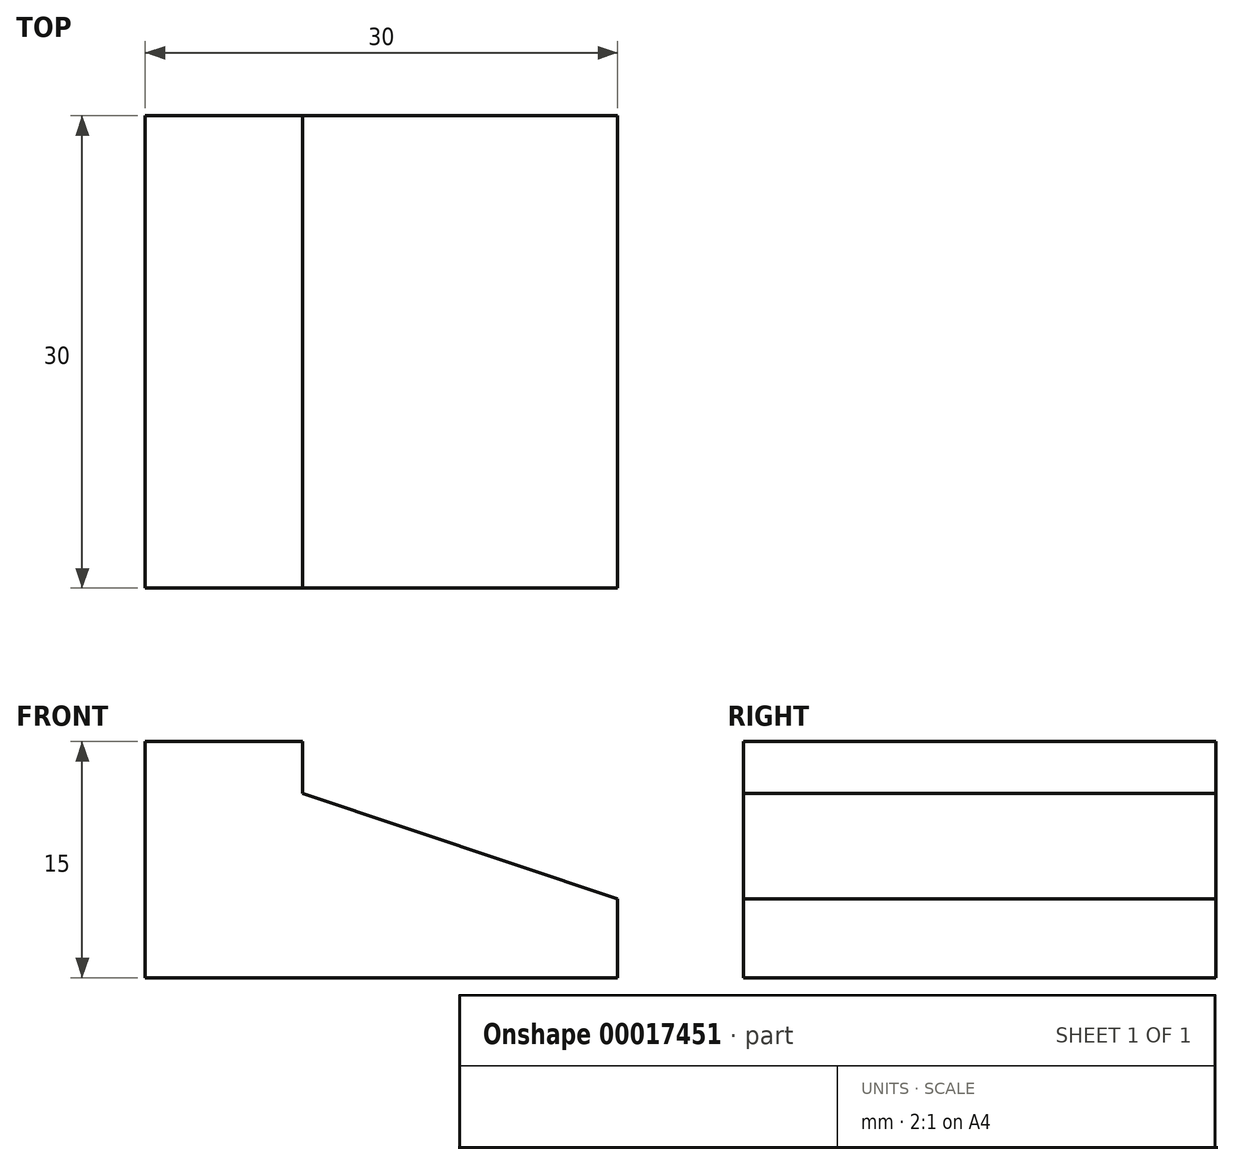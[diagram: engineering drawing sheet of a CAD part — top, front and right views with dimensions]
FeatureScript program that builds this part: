
annotation { "Feature Type Name" : "Feature", "Feature Type Description" : "" }
export const myFeature = defineFeature(function(context is Context, id is Id, definition is map)
    precondition{}
    {
        {
            var Q0;
            Q0=qCreatedBy(makeId("Front.planeOp"),FACE);
            var sketch = newSketch(context, id + "F0", { "sketchPlane" : qUnion([Q0])});
            skLineSegment(sketch, "E0", {"start": v(-16.89, 15) * mm, "end": v(-16.89, 0) * mm});
            skLineSegment(sketch, "E1", {"start": v(-16.89, 15) * mm, "end": v(-6.89, 15) * mm});
            skLineSegment(sketch, "E2", {"start": v(-16.89, 0) * mm, "end": v(13.11, 0) * mm});
            skLineSegment(sketch, "E3", {"start": v(-6.89, 15) * mm, "end": v(-6.89, 11.72) * mm});
            skLineSegment(sketch, "E4", {"start": v(13.11, 0) * mm, "end": v(13.11, 5) * mm});
            skLineSegment(sketch, "E5", {"start": v(-6.89, 11.72) * mm, "end": v(13.11, 5) * mm});
            skSolve(sketch);
        }
        {
            var Q0;
            Q0=makeQuery(id+"F0.imprint","IMPRINT",FACE,{"disambiguationData":[TD([[makeQuery(id+"F0.imprint","IMPRINT",EDGE,{"derivedFrom":sQuery(id+"F0.wireOp",EDGE,"E0")}),1.0]])]});
            extrude(context, id + "F1", {"entities" : qUnion([Q0]), "depth" : 30 * mm});
        }
    });
